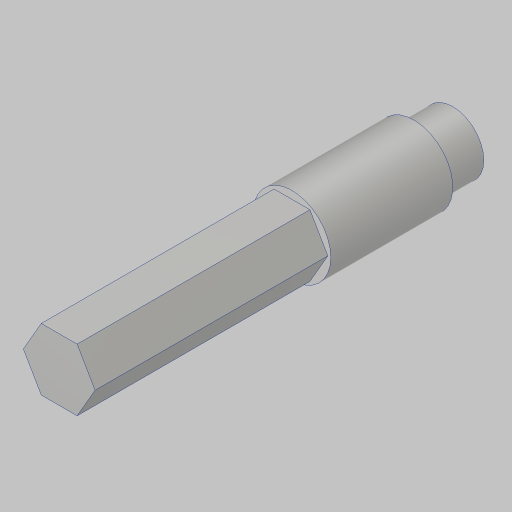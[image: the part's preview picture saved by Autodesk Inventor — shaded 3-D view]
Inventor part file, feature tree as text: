
AUTODESK INVENTOR PART (.ipt)
format: ipt  version: 2023.5 (Build 275446000, 446)  size: 148,480 bytes
history: native  units: in
note: dims shown in document units (in); Inventor stores cm internally (conversion verified against a paired STEP export)
features: extrude x5, sketch x5, projected_geometry x5
ambient origin geometry x8: Origin, YZ Plane, XZ Plane, XY Plane, X Axis, Y Axis, Z Axis, Center Point
bodies: Solid1 (feature_tree)
feature tree (15):
  extrude  "Extrusion1"  Depth=3.5625in TaperAngle=0.0deg
  extrude  "Extrusion2"  Depth=0.5in TaperAngle=0.0deg
  extrude  "Extrusion3"  Depth=0.25in TaperAngle=0.0deg
  extrude  "Extrusion6"  TaperAngle=0.0deg  [1 undecoded]
  extrude  "Extrusion7"  Depth=0.3125in TaperAngle=0.0deg
  sketch  "Sketch1"  dims[d0=0.625in d1=3.5625in d2=0.0in]
  sketch  "Sketch2"  dims[d3=0.5in d4=2.125in d5=0.0in]
  projected_geometry  "Projected Loop1"
  sketch  "Sketch3"  dims[d6=0.5in d7=0.25in d8=0.0in]
  projected_geometry  "Projected Loop2"
  sketch  "Sketch6"  dims[d15=3.17in d16=0.0in d17=0.0in]
  sketch  "Sketch7"  dims[d18=0.5in d19=0.3125in d20=0.0in]
  projected_geometry  "Project Cut Edges3"
  projected_geometry  "Project Cut Edges4"
  projected_geometry  "Project Cut Edges5"
note: 1 required parameter value undecoded (feature->parameter linkage not recoverable at this tier; creation-order binding heuristic only, values carry confidence <= 0.55)
